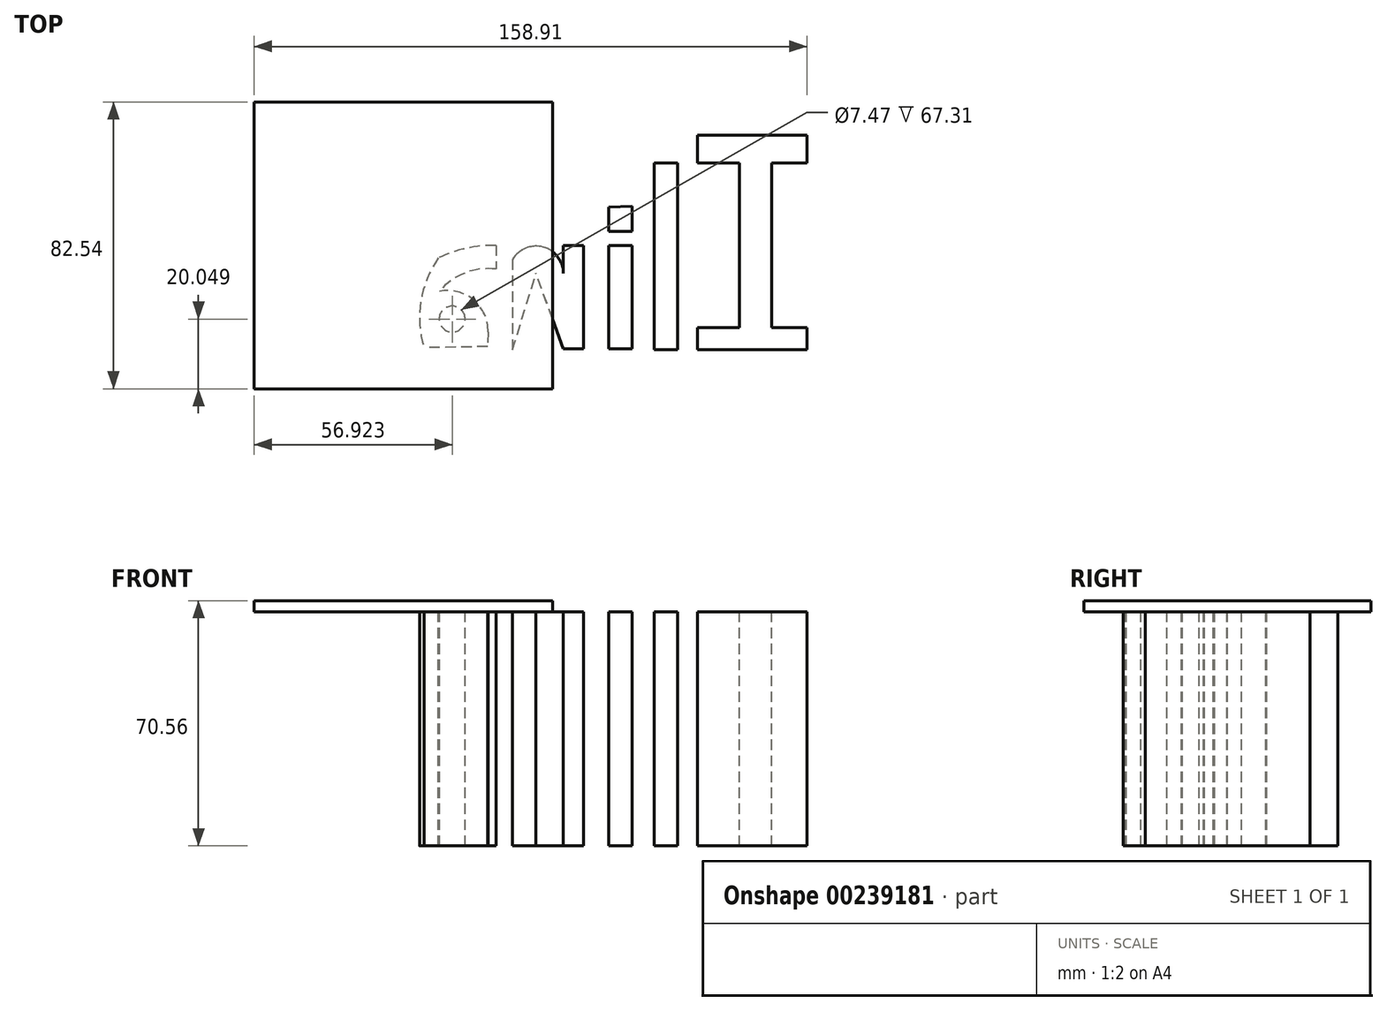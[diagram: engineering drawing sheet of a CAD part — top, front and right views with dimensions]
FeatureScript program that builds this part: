
annotation { "Feature Type Name" : "Feature", "Feature Type Description" : "" }
export const myFeature = defineFeature(function(context is Context, id is Id, definition is map)
    precondition{}
    {
        {
            assignVariable(context, id + "F0", {"name" : "T", "anyValue" : 3.25});
        }
        {
            var Q0;
            Q0=qCreatedBy(makeId("Top.planeOp"),FACE);
            var sketch = newSketch(context, id + "F1", { "sketchPlane" : qUnion([Q0])});
            skLineSegment(sketch, "E0.bottom", {"start": v(-41.27, 41.28) * mm, "end": v(41.28, 41.28) * mm});
            skLineSegment(sketch, "E0.top", {"start": v(-41.28, -41.28) * mm, "end": v(41.27, -41.28) * mm});
            skLineSegment(sketch, "E0.left", {"start": v(-41.27, 41.28) * mm, "end": v(-41.28, -41.28) * mm});
            skLineSegment(sketch, "E0.right", {"start": v(41.28, 41.28) * mm, "end": v(41.28, -41.28) * mm});
            skPoint(sketch, "E0.middle", {"position": v(0, 0) * mm});
            skSolve(sketch);
        }
        {
            var Q0;
            Q0=makeQuery(id+"F1.imprint","IMPRINT",FACE,{"disambiguationData":[TD([[makeQuery(id+"F1.imprint","IMPRINT",EDGE,{"derivedFrom":sQuery(id+"F1.wireOp",EDGE,"E0.bottom")}),-1.0]])]});
            extrude(context, id + "F2", {"entities" : qUnion([Q0]), "endBound" : BoundingType.SYMMETRIC, "depth" : (getVariable(context, 'T')) * mm});
        }
        {
            var Q0;
            Q0=makeQuery(id+"F2.opExtrude","SWEPT_FACE",FACE,{"disambiguationData":[OSD([sQuery(id+"F1.wireOp",EDGE,"E0.right")])]});
            extrude(context, id + "F3", {"entities" : qUnion([Q0]), "operationType" : NewBodyOperationType.ADD, "depth" : (getVariable(context, 'T')) * mm});
        }
        {
            var Q0;
            {var subQ0=sQuery(id+"F1.wireOp",EDGE,"E0.right");Q0=makeQuery(id+"F3.boolean.opBoolean","MERGE",FACE,{"derivedFrom":[makeQuery(id+"F2.opExtrude","CAP_FACE",FACE,{"disambiguationData":[OSD([sQuery(id+"F1.wireOp",EDGE,"E0.bottom"),sQuery(id+"F1.wireOp",EDGE,"E0.top"),sQuery(id+"F1.wireOp",EDGE,"E0.left"),subQ0])],"isStart":true}),makeQuery(id+"F3.opExtrude","SWEPT_FACE",FACE,{"disambiguationData":[OSD([subQ0]),TDD([makeQuery(id+"F2.opExtrude","CAP_EDGE",EDGE,{"disambiguationData":[OSD([subQ0])],"isStart":true})])]})]});}
            var sketch = newSketch(context, id + "F4", { "sketchPlane" : qUnion([Q0])});
            skLineSegment(sketch, "E1", {"start": v(107.46, -23.7) * mm, "end": v(107.46, 23.7) * mm});
            skLineSegment(sketch, "E2", {"start": v(107.46, 23.7) * mm, "end": v(117.64, 23.7) * mm});
            skLineSegment(sketch, "E3", {"start": v(117.64, 23.7) * mm, "end": v(117.64, 30.07) * mm});
            skLineSegment(sketch, "E4", {"start": v(117.64, 30.07) * mm, "end": v(86.14, 30.07) * mm});
            skLineSegment(sketch, "E5", {"start": v(86.14, 30.07) * mm, "end": v(86.14, 23.7) * mm});
            skLineSegment(sketch, "E6", {"start": v(86.14, 23.7) * mm, "end": v(98.23, 23.7) * mm});
            skLineSegment(sketch, "E7", {"start": v(98.23, 23.7) * mm, "end": v(98.23, -23.7) * mm});
            skLineSegment(sketch, "E8", {"start": v(98.23, -23.7) * mm, "end": v(86.14, -23.7) * mm});
            skLineSegment(sketch, "E9", {"start": v(86.14, -23.7) * mm, "end": v(86.14, -31.66) * mm});
            skLineSegment(sketch, "E10", {"start": v(86.14, -31.66) * mm, "end": v(117.64, -31.66) * mm});
            skLineSegment(sketch, "E11", {"start": v(117.64, -31.66) * mm, "end": v(117.64, -23.7) * mm});
            skLineSegment(sketch, "E12", {"start": v(117.64, -23.7) * mm, "end": v(107.46, -23.7) * mm});
            skLineSegment(sketch, "E13", {"start": v(80.41, -23.7) * mm, "end": v(80.41, 30.07) * mm});
            skLineSegment(sketch, "E14", {"start": v(80.41, 30.07) * mm, "end": v(73.73, 30.07) * mm});
            skLineSegment(sketch, "E15", {"start": v(73.73, 30.07) * mm, "end": v(73.73, -23.7) * mm});
            skLineSegment(sketch, "E16", {"start": v(73.73, -23.7) * mm, "end": v(80.41, -23.7) * mm});
            skLineSegment(sketch, "E17", {"start": v(67.37, 0) * mm, "end": v(67.37, 29.75) * mm});
            skLineSegment(sketch, "E18", {"start": v(67.37, 29.75) * mm, "end": v(60.69, 29.75) * mm});
            skLineSegment(sketch, "E19", {"start": v(60.69, 29.75) * mm, "end": v(60.69, 0) * mm});
            skLineSegment(sketch, "E20", {"start": v(60.69, 0) * mm, "end": v(67.37, 0) * mm});
            skLineSegment(sketch, "E21", {"start": v(67.37, -11.3) * mm, "end": v(67.37, -3.98) * mm});
            skLineSegment(sketch, "E22", {"start": v(67.37, -3.98) * mm, "end": v(60.69, -3.98) * mm});
            skLineSegment(sketch, "E23", {"start": v(60.69, -3.98) * mm, "end": v(60.69, -10.98) * mm});
            skLineSegment(sketch, "E24", {"start": v(60.69, -10.98) * mm, "end": v(67.37, -11.3) * mm});
            skLineSegment(sketch, "E25", {"start": v(53.37, 0) * mm, "end": v(53.37, 29.75) * mm});
            skLineSegment(sketch, "E26", {"start": v(53.37, 0) * mm, "end": v(47.64, 0) * mm});
            skLineSegment(sketch, "E27", {"start": v(47.64, 0) * mm, "end": v(47.64, 8.11) * mm});
            skLineSegment(sketch, "E28", {"start": v(53.37, 29.75) * mm, "end": v(47.64, 29.75) * mm});
            skArc(sketch, "E29", {"start": v(33, 4.06) * mm, "mid": v(41.86, 0.52) * mm, "end": v(47.64, 8.11) * mm});
            skPoint(sketch, "E29.startSnap0", {"position": v(47.64, 4.06) * mm});
            skLineSegment(sketch, "E30", {"start": v(33, 4.06) * mm, "end": v(33, 30.07) * mm});
            skLineSegment(sketch, "E31", {"start": v(33, 30.07) * mm, "end": v(39.76, 8.11) * mm});
            skLineSegment(sketch, "E32", {"start": v(47.64, 29.75) * mm, "end": v(39.76, 8.11) * mm});
            skArc(sketch, "E33", {"start": v(11.68, 3.66) * mm, "mid": v(19.74, 0.86) * mm, "end": v(28.23, 0) * mm});
            skArc(sketch, "E34", {"start": v(7.55, 29.43) * mm, "mid": v(6.65, 16.07) * mm, "end": v(11.68, 3.66) * mm});
            skLineSegment(sketch, "E35", {"start": v(12, 29.43) * mm, "end": v(7.55, 29.43) * mm});
            skLineSegment(sketch, "E36", {"start": v(28.23, 0) * mm, "end": v(28.23, 6.84) * mm});
            skArc(sketch, "E37", {"start": v(12, 13.2) * mm, "mid": v(19.3, 7.96) * mm, "end": v(28.23, 6.84) * mm});
            skArc(sketch, "E38", {"start": v(12, 13.2) * mm, "mid": v(21.8, 15.73) * mm, "end": v(25.97, 24.94) * mm});
            skLineSegment(sketch, "E39", {"start": v(25.97, 24.94) * mm, "end": v(25.87, 29.15) * mm});
            skLineSegment(sketch, "E40", {"start": v(25.87, 29.15) * mm, "end": v(7.55, 29.43) * mm});
            skCircle(sketch, "E41", {"center": v(15.65, 21.22) * mm, "radius": 3.73 * mm});
            skPoint(sketch, "E41.first.point", {"position": v(16.77, 17.66) * mm});
            skPoint(sketch, "E41.third.point", {"position": v(19, 19.57) * mm});
            skSolve(sketch);
        }
        {
            var Q0;
            Q0 = qSketchRegion(id + "F4", true);
            extrude(context, id + "F5", {"entities" : qUnion([Q0]), "operationType" : NewBodyOperationType.ADD, "depth" : 67.3 * mm});
        }
    });
